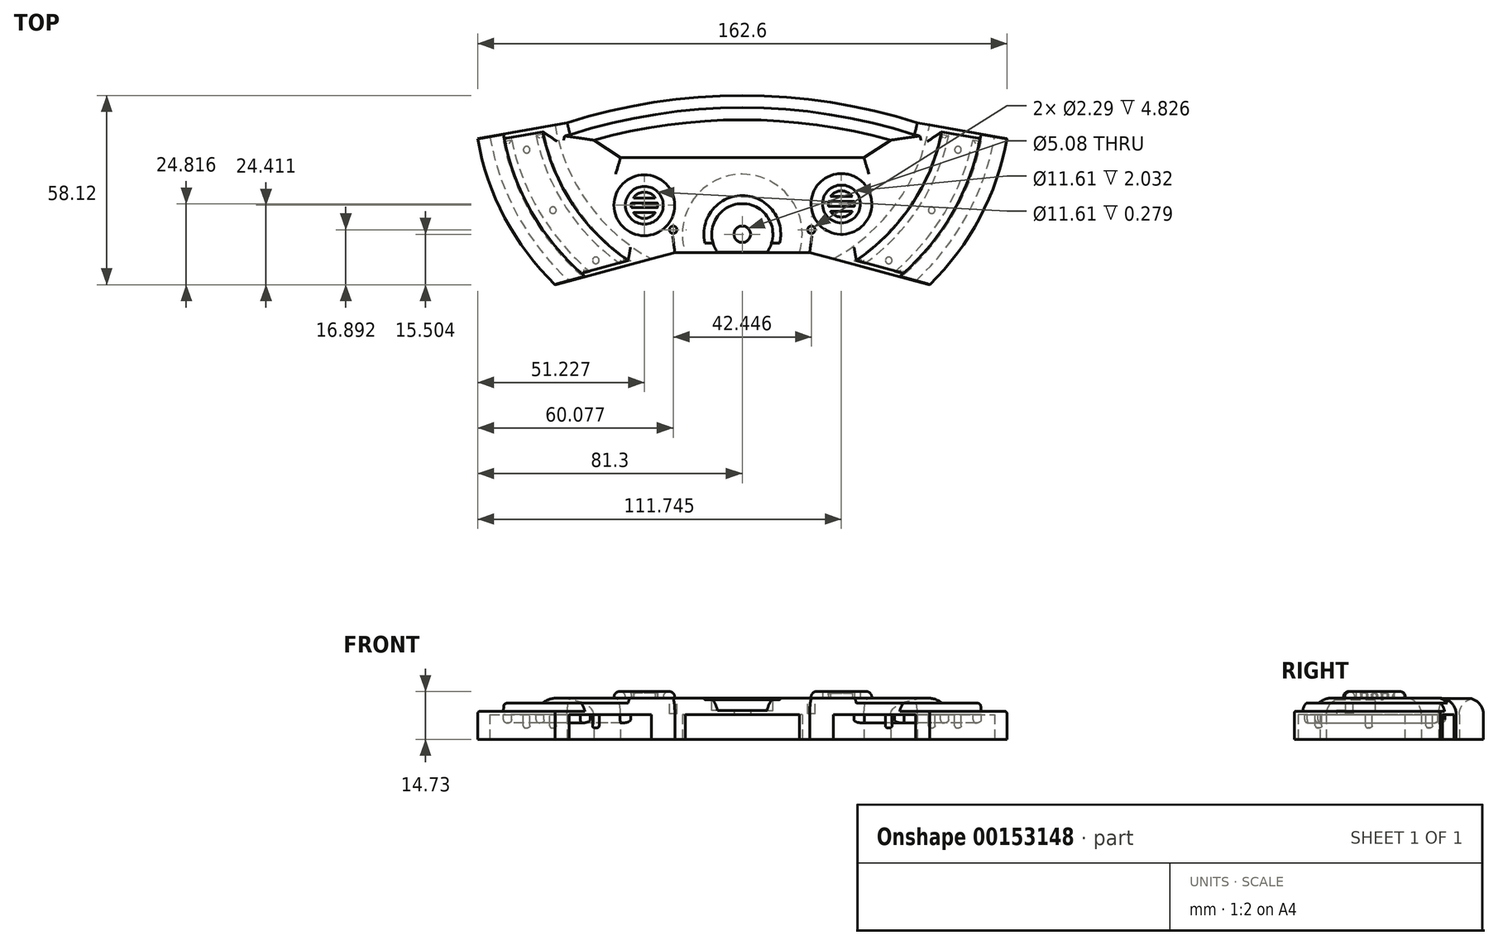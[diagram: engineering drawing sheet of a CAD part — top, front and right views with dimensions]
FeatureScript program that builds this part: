
annotation { "Feature Type Name" : "Feature", "Feature Type Description" : "" }
export const myFeature = defineFeature(function(context is Context, id is Id, definition is map)
    precondition{}
    {
        {
            var Q0;
            Q0=qCreatedBy(makeId("Top.planeOp"),FACE);
            var sketch = newSketch(context, id + "F0", { "sketchPlane" : qUnion([Q0])});
            skCircle(sketch, "E0", {"center": v(0, 0) * mm, "radius": 76.2 * mm, "construction": true});
            skCircle(sketch, "E1", {"center": v(0, 0) * mm, "radius": 60.96 * mm, "construction": true});
            skArc(sketch, "E2", {"start": v(-81.3, -14.33) * mm, "mid": v(-72.94, -38.65) * mm, "end": v(-57.5, -59.22) * mm});
            skLineSegment(sketch, "E3", {"start": v(0, 0) * mm, "end": v(-81.3, -14.33) * mm, "construction": true});
            skArc(sketch, "E4", {"start": v(81.3, -14.33) * mm, "mid": v(72.94, -38.65) * mm, "end": v(57.5, -59.22) * mm});
            skLineSegment(sketch, "E5", {"start": v(81.3, -14.33) * mm, "end": v(0, 0) * mm, "construction": true});
            skLineSegment(sketch, "E6", {"start": v(81.3, -14.33) * mm, "end": v(57.5, -59.22) * mm, "construction": true});
            skLineSegment(sketch, "E7", {"start": v(-81.3, -14.33) * mm, "end": v(-57.5, -59.22) * mm, "construction": true});
            skLineSegment(sketch, "E8", {"start": v(57.5, -59.22) * mm, "end": v(20.7, -49.36) * mm});
            skLineSegment(sketch, "E9", {"start": v(20.7, -49.36) * mm, "end": v(-20.7, -49.36) * mm});
            skLineSegment(sketch, "E10", {"start": v(-20.7, -49.36) * mm, "end": v(-57.5, -59.22) * mm});
            skLineSegment(sketch, "E11", {"start": v(-81.3, -14.33) * mm, "end": v(-53.78, -9.48) * mm});
            skLineSegment(sketch, "E12", {"start": v(-45.58, -14.8) * mm, "end": v(-37.38, -20.13) * mm});
            skLineSegment(sketch, "E13", {"start": v(-37.38, -20.13) * mm, "end": v(37.38, -20.13) * mm});
            skLineSegment(sketch, "E14", {"start": v(37.38, -20.13) * mm, "end": v(45.58, -14.8) * mm});
            skLineSegment(sketch, "E15", {"start": v(53.78, -9.48) * mm, "end": v(81.3, -14.33) * mm});
            skLineSegment(sketch, "E16", {"start": v(0, 0) * mm, "end": v(0, -177.8) * mm, "construction": true});
            skArc(sketch, "E17", {"start": v(-53.78, -9.48) * mm, "mid": v(0, -1.1) * mm, "end": v(53.78, -9.48) * mm});
            skArc(sketch, "E18", {"start": v(45.58, -14.8) * mm, "mid": v(0, -8.56) * mm, "end": v(-45.58, -14.8) * mm});
            skSolve(sketch);
        }
        {
            var Q0;
            Q0=qSketchRegion(id+"F0",true);
            extrude(context, id + "F1", {"entities" : qUnion([Q0]), "depth" : 12.7 * mm});
        }
        {
            var Q0;
            Q0=qCreatedBy(makeId("Front.planeOp"),FACE);
            var sketch = newSketch(context, id + "F2", { "sketchPlane" : qUnion([Q0])});
            skLineSegment(sketch, "E19", {"start": v(62.5, 16.37) * mm, "end": v(62.5, 11.1) * mm});
            skLineSegment(sketch, "E20", {"start": v(62.5, 11.1) * mm, "end": v(74.5, 11.1) * mm});
            skLineSegment(sketch, "E21", {"start": v(74.5, 11.1) * mm, "end": v(74.5, 8.65) * mm});
            skLineSegment(sketch, "E22", {"start": v(74.5, 8.65) * mm, "end": v(83.99, 8.65) * mm});
            skLineSegment(sketch, "E23", {"start": v(83.99, 8.65) * mm, "end": v(83.99, 15.75) * mm});
            skLineSegment(sketch, "E24", {"start": v(83.99, 15.75) * mm, "end": v(62.5, 16.37) * mm});
            skSolve(sketch);
        }
        {
            var Q0;
            Q0=qCreatedBy(makeId("Front.planeOp"),FACE);
            var sketch = newSketch(context, id + "F3", { "sketchPlane" : qUnion([Q0])});
            skLineSegment(sketch, "E25", {"start": v(0, 99.5) * mm, "end": v(0, -112.08) * mm, "construction": true});
            skSolve(sketch);
        }
        {
            var Q0;
            Q0=qSketchRegion(id+"F2",true);
            var Q1;
            Q1=sQuery(id+"F3.wireOp",EDGE,"E25");
            revolve(context, id + "F4", {"operationType" : NewBodyOperationType.REMOVE, "entities" : qUnion([Q0]), "axis" : qUnion([Q1]), "revolveType" : RevolveType.FULL, "oppositeDirection" : true});
        }
        {
            var Q0;
            Q0=makeQuery(id+"F1.opExtrude","CAP_FACE",FACE,{"disambiguationData":[OSD([sQuery(id+"F0.wireOp",EDGE,"E2"),sQuery(id+"F0.wireOp",EDGE,"E4"),sQuery(id+"F0.wireOp",EDGE,"E8"),sQuery(id+"F0.wireOp",EDGE,"E9"),sQuery(id+"F0.wireOp",EDGE,"E10"),sQuery(id+"F0.wireOp",EDGE,"E11"),sQuery(id+"F0.wireOp",EDGE,"E12"),sQuery(id+"F0.wireOp",EDGE,"E13"),sQuery(id+"F0.wireOp",EDGE,"E14"),sQuery(id+"F0.wireOp",EDGE,"E15"),sQuery(id+"F0.wireOp",EDGE,"E17"),sQuery(id+"F0.wireOp",EDGE,"E18")])],"isStart":false});
            fillet(context, id + "F5", {"entities" : qUnion([Q0]), "radius" : 5.08 * mm, "tangentPropagation" : true, "allowEdgeOverflow" : false});
        }
        {
            var Q0;
            Q0=makeQuery(id+"F1.opExtrude","CAP_FACE",FACE,{"disambiguationData":[OSD([sQuery(id+"F0.wireOp",EDGE,"E2"),sQuery(id+"F0.wireOp",EDGE,"E4"),sQuery(id+"F0.wireOp",EDGE,"E8"),sQuery(id+"F0.wireOp",EDGE,"E9"),sQuery(id+"F0.wireOp",EDGE,"E10"),sQuery(id+"F0.wireOp",EDGE,"E11"),sQuery(id+"F0.wireOp",EDGE,"E12"),sQuery(id+"F0.wireOp",EDGE,"E13"),sQuery(id+"F0.wireOp",EDGE,"E14"),sQuery(id+"F0.wireOp",EDGE,"E15"),sQuery(id+"F0.wireOp",EDGE,"E17"),sQuery(id+"F0.wireOp",EDGE,"E18")])],"isStart":false});
            var sketch = newSketch(context, id + "F6", { "sketchPlane" : qUnion([Q0])});
            skLineSegment(sketch, "E26", {"start": v(38.88, -25.21) * mm, "end": v(34.33, -47.75) * mm, "construction": true});
            skLineSegment(sketch, "E27", {"start": v(34.33, -47.75) * mm, "end": v(56.82, -15.18) * mm, "construction": true});
            skLineSegment(sketch, "E28", {"start": v(56.82, -15.18) * mm, "end": v(-56.82, -15.18) * mm, "construction": true});
            skLineSegment(sketch, "E29", {"start": v(-56.82, -15.18) * mm, "end": v(-34.33, -47.75) * mm, "construction": true});
            skLineSegment(sketch, "E30", {"start": v(-34.33, -47.75) * mm, "end": v(-38.88, -25.21) * mm, "construction": true});
            skLineSegment(sketch, "E31", {"start": v(-38.88, -25.21) * mm, "end": v(46.13, -36.48) * mm, "construction": true});
            skPoint(sketch, "E31.endSnap0", {"position": v(-36.6, -36.48) * mm});
            skLineSegment(sketch, "E32", {"start": v(46.13, -36.48) * mm, "end": v(-42.1, -36.48) * mm, "construction": true});
            skLineSegment(sketch, "E33", {"start": v(-42.1, -36.48) * mm, "end": v(38.88, -25.21) * mm, "construction": true});
            skLineSegment(sketch, "E34", {"start": v(21.38, -44.28) * mm, "end": v(38.88, -25.21) * mm, "construction": true});
            skLineSegment(sketch, "E35", {"start": v(-21.38, -44.28) * mm, "end": v(-38.88, -25.21) * mm, "construction": true});
            skCircle(sketch, "E36", {"center": v(30.44, -34.4) * mm, "radius": 9.33 * mm});
            skCircle(sketch, "E37", {"center": v(-30.07, -34.8) * mm, "radius": 9.33 * mm});
            skCircle(sketch, "E38", {"center": v(-30.07, -34.8) * mm, "radius": 5.8 * mm});
            skCircle(sketch, "E39", {"center": v(30.44, -34.4) * mm, "radius": 5.8 * mm});
            skSolve(sketch);
        }
        {
            var Q0;
            Q0=qSketchRegion(id+"F6",true);
            extrude(context, id + "F7", {"entities" : qUnion([Q0]), "operationType" : NewBodyOperationType.ADD, "depth" : 2.03 * mm});
        }
        {
            var Q0;
            Q0=makeQuery(id+"F7.opExtrude","CAP_FACE",FACE,{"disambiguationData":[OSD([sQuery(id+"F6.wireOp",EDGE,"E37"),sQuery(id+"F6.wireOp",EDGE,"E38")])],"isStart":false});
            var Q1;
            Q1=makeQuery(id+"F7.opExtrude","CAP_EDGE",EDGE,{"disambiguationData":[OSD([sQuery(id+"F6.wireOp",EDGE,"E36")])],"isStart":false});
            fillet(context, id + "F8", {"entities" : qUnion([Q0, Q1]), "radius" : 1.75 * mm, "tangentPropagation" : true, "allowEdgeOverflow" : false});
        }
        {
            var Q0;
            Q0=makeQuery(id+"F7.boolean.opBoolean","SPLIT",FACE,{"disambiguationData":[TD([makeQuery(id+"F7.opExtrude","SWEPT_FACE",FACE,{"disambiguationData":[OSD([sQuery(id+"F6.wireOp",EDGE,"E38")])]})])],"derivedFrom":makeQuery(id+"F1.opExtrude","CAP_FACE",FACE,{"disambiguationData":[OSD([sQuery(id+"F0.wireOp",EDGE,"E2"),sQuery(id+"F0.wireOp",EDGE,"E4"),sQuery(id+"F0.wireOp",EDGE,"E8"),sQuery(id+"F0.wireOp",EDGE,"E9"),sQuery(id+"F0.wireOp",EDGE,"E10"),sQuery(id+"F0.wireOp",EDGE,"E11"),sQuery(id+"F0.wireOp",EDGE,"E12"),sQuery(id+"F0.wireOp",EDGE,"E13"),sQuery(id+"F0.wireOp",EDGE,"E14"),sQuery(id+"F0.wireOp",EDGE,"E15"),sQuery(id+"F0.wireOp",EDGE,"E17"),sQuery(id+"F0.wireOp",EDGE,"E18")])],"isStart":false})});
            var sketch = newSketch(context, id + "F9", { "sketchPlane" : qUnion([Q0])});
            skArc(sketch, "E40", {"start": v(-34.04, -34.07) * mm, "mid": v(-34.11, -34.8) * mm, "end": v(-34.04, -35.55) * mm});
            skLineSegment(sketch, "E41", {"start": v(-26.73, -32.55) * mm, "end": v(-33.42, -32.55) * mm});
            skLineSegment(sketch, "E42", {"start": v(-26.1, -34.07) * mm, "end": v(-34.04, -34.07) * mm});
            skLineSegment(sketch, "E43", {"start": v(-26.1, -35.55) * mm, "end": v(-34.04, -35.55) * mm});
            skLineSegment(sketch, "E44", {"start": v(-33.42, -37.07) * mm, "end": v(-26.73, -37.07) * mm});
            skArc(sketch, "E45.trimOffspring", {"start": v(-26.73, -32.55) * mm, "mid": v(-30.07, -30.77) * mm, "end": v(-33.42, -32.55) * mm});
            skArc(sketch, "E46.trimOffspring", {"start": v(-26.1, -35.55) * mm, "mid": v(-26.03, -34.8) * mm, "end": v(-26.1, -34.07) * mm});
            skArc(sketch, "E47.trimOffspring", {"start": v(-33.42, -37.07) * mm, "mid": v(-30.07, -38.85) * mm, "end": v(-26.73, -37.07) * mm});
            skSolve(sketch);
        }
        {
            var Q0;
            Q0=makeQuery(id+"F7.boolean.opBoolean","SPLIT",FACE,{"disambiguationData":[TD([makeQuery(id+"F7.opExtrude","SWEPT_FACE",FACE,{"disambiguationData":[OSD([sQuery(id+"F6.wireOp",EDGE,"E39")])]})])],"derivedFrom":makeQuery(id+"F1.opExtrude","CAP_FACE",FACE,{"disambiguationData":[OSD([sQuery(id+"F0.wireOp",EDGE,"E2"),sQuery(id+"F0.wireOp",EDGE,"E4"),sQuery(id+"F0.wireOp",EDGE,"E8"),sQuery(id+"F0.wireOp",EDGE,"E9"),sQuery(id+"F0.wireOp",EDGE,"E10"),sQuery(id+"F0.wireOp",EDGE,"E11"),sQuery(id+"F0.wireOp",EDGE,"E12"),sQuery(id+"F0.wireOp",EDGE,"E13"),sQuery(id+"F0.wireOp",EDGE,"E14"),sQuery(id+"F0.wireOp",EDGE,"E15"),sQuery(id+"F0.wireOp",EDGE,"E17"),sQuery(id+"F0.wireOp",EDGE,"E18")])],"isStart":false})});
            var sketch = newSketch(context, id + "F10", { "sketchPlane" : qUnion([Q0])});
            skArc(sketch, "E48", {"start": v(33.8, -32.14) * mm, "mid": v(30.44, -30.37) * mm, "end": v(27.1, -32.14) * mm});
            skLineSegment(sketch, "E49", {"start": v(27.1, -32.14) * mm, "end": v(33.8, -32.14) * mm});
            skLineSegment(sketch, "E50", {"start": v(34.42, -33.67) * mm, "end": v(26.47, -33.67) * mm});
            skLineSegment(sketch, "E51", {"start": v(26.47, -35.14) * mm, "end": v(34.42, -35.14) * mm});
            skLineSegment(sketch, "E52", {"start": v(33.8, -36.67) * mm, "end": v(27.1, -36.67) * mm});
            skArc(sketch, "E53.trimOffspring", {"start": v(26.47, -33.67) * mm, "mid": v(26.4, -34.4) * mm, "end": v(26.47, -35.14) * mm});
            skArc(sketch, "E54.trimOffspring", {"start": v(27.1, -36.67) * mm, "mid": v(30.44, -38.44) * mm, "end": v(33.8, -36.67) * mm});
            skArc(sketch, "E55.trimOffspring", {"start": v(34.42, -35.14) * mm, "mid": v(34.48, -34.4) * mm, "end": v(34.42, -33.67) * mm});
            skSolve(sketch);
        }
        {
            var Q0;
            Q0=qSketchRegion(id+"F9",true);
            extrude(context, id + "F11", {"entities" : qUnion([Q0]), "operationType" : NewBodyOperationType.ADD, "depth" : 1.52 * mm});
        }
        {
            var Q0;
            Q0=makeQuery(id+"F11.opExtrude","CAP_EDGE",EDGE,{"disambiguationData":[OSD([sQuery(id+"F9.wireOp",EDGE,"E42")])],"isStart":false});
            var Q1;
            Q1=makeQuery(id+"F11.opExtrude","CAP_EDGE",EDGE,{"disambiguationData":[OSD([sQuery(id+"F9.wireOp",EDGE,"E43")])],"isStart":false});
            fillet(context, id + "F12", {"entities" : qUnion([Q0, Q1]), "radius" : 0.7 * mm, "tangentPropagation" : true, "allowEdgeOverflow" : false});
        }
        {
            var Q0;
            Q0=makeQuery(id+"F11.opExtrude","CAP_FACE",FACE,{"disambiguationData":[OSD([sQuery(id+"F9.wireOp",EDGE,"E41"),sQuery(id+"F9.wireOp",EDGE,"E45.trimOffspring")])],"isStart":false});
            var Q1;
            Q1=makeQuery(id+"F11.opExtrude","CAP_FACE",FACE,{"disambiguationData":[OSD([sQuery(id+"F9.wireOp",EDGE,"E44"),sQuery(id+"F9.wireOp",EDGE,"E47.trimOffspring")])],"isStart":false});
            fillet(context, id + "F13", {"entities" : qUnion([Q0, Q1]), "radius" : 0.25 * mm, "tangentPropagation" : true, "allowEdgeOverflow" : false});
        }
        {
            var Q0;
            Q0=qSketchRegion(id+"F10",true);
            extrude(context, id + "F14", {"entities" : qUnion([Q0]), "operationType" : NewBodyOperationType.ADD, "depth" : 1.52 * mm});
        }
        {
            var Q0;
            Q0=makeQuery(id+"F4.boolean.opBoolean","COPY",EDGE,{"disambiguationData":[OD(1.0)],"derivedFrom":makeQuery(id+"F4.opRevolve","SWEPT_EDGE",EDGE,{"disambiguationData":[OSD([sQuery(id+"F2.wireOp",EDGE,"E20"),sQuery(id+"F2.wireOp",EDGE,"E21")])]})});
            var Q1;
            Q1=makeQuery(id+"F4.boolean.opBoolean","INTERSECT",EDGE,{"derivedFrom":[makeQuery(id+"F1.opExtrude","SWEPT_FACE",FACE,{"disambiguationData":[OSD([sQuery(id+"F0.wireOp",EDGE,"E2")])]}),makeQuery(id+"F4.opRevolve","SWEPT_FACE",FACE,{"disambiguationData":[OSD([sQuery(id+"F2.wireOp",EDGE,"E22")])]})]});
            var Q2;
            Q2=makeQuery(id+"F4.boolean.opBoolean","COPY",EDGE,{"disambiguationData":[OD(0.0)],"derivedFrom":makeQuery(id+"F4.opRevolve","SWEPT_EDGE",EDGE,{"disambiguationData":[OSD([sQuery(id+"F2.wireOp",EDGE,"E20"),sQuery(id+"F2.wireOp",EDGE,"E21")])]})});
            var Q3;
            Q3=makeQuery(id+"F4.boolean.opBoolean","INTERSECT",EDGE,{"derivedFrom":[makeQuery(id+"F1.opExtrude","SWEPT_FACE",FACE,{"disambiguationData":[OSD([sQuery(id+"F0.wireOp",EDGE,"E4")])]}),makeQuery(id+"F4.opRevolve","SWEPT_FACE",FACE,{"disambiguationData":[OSD([sQuery(id+"F2.wireOp",EDGE,"E22")])]})]});
            fillet(context, id + "F15", {"entities" : qUnion([Q0, Q1, Q2, Q3]), "radius" : 0.76 * mm, "tangentPropagation" : true, "allowEdgeOverflow" : false});
        }
        {
            var Q0;
            Q0=qCreatedBy(makeId("Top.planeOp"),FACE);
            var sketch = newSketch(context, id + "F16", { "sketchPlane" : qUnion([Q0])});
            skCircle(sketch, "E56", {"center": v(0, 0) * mm, "radius": 78.74 * mm});
            skCircle(sketch, "E57", {"center": v(0, 0) * mm, "radius": 58.42 * mm});
            skSolve(sketch);
        }
        {
            var Q0;
            Q0=qSketchRegion(id+"F16",true);
            extrude(context, id + "F17", {"entities" : qUnion([Q0]), "operationType" : NewBodyOperationType.REMOVE, "depth" : 7.62 * mm});
        }
        {
            var Q0;
            Q0=makeQuery(id+"F14.opExtrude","CAP_EDGE",EDGE,{"disambiguationData":[OSD([sQuery(id+"F10.wireOp",EDGE,"E50")])],"isStart":false});
            var Q1;
            Q1=makeQuery(id+"F14.opExtrude","CAP_EDGE",EDGE,{"disambiguationData":[OSD([sQuery(id+"F10.wireOp",EDGE,"E51")])],"isStart":false});
            fillet(context, id + "F18", {"entities" : qUnion([Q0, Q1]), "radius" : 0.71 * mm, "tangentPropagation" : true, "allowEdgeOverflow" : false});
        }
        {
            var Q0;
            Q0=makeQuery(id+"F14.opExtrude","CAP_FACE",FACE,{"disambiguationData":[OSD([sQuery(id+"F10.wireOp",EDGE,"E48"),sQuery(id+"F10.wireOp",EDGE,"E49")])],"isStart":false});
            var Q1;
            Q1=makeQuery(id+"F14.opExtrude","CAP_FACE",FACE,{"disambiguationData":[OSD([sQuery(id+"F10.wireOp",EDGE,"E52"),sQuery(id+"F10.wireOp",EDGE,"E54.trimOffspring")])],"isStart":false});
            fillet(context, id + "F19", {"entities" : qUnion([Q0, Q1]), "radius" : 0.25 * mm, "tangentPropagation" : true, "allowEdgeOverflow" : false});
        }
        {
            var Q0;
            Q0=makeQuery(id+"F17.boolean.opBoolean","COPY",FACE,{"disambiguationData":[OD(1.0)],"derivedFrom":makeQuery(id+"F17.opExtrude","CAP_FACE",FACE,{"disambiguationData":[OSD([sQuery(id+"F16.wireOp",EDGE,"E56"),sQuery(id+"F16.wireOp",EDGE,"E57")])],"isStart":false})});
            var sketch = newSketch(context, id + "F20", { "sketchPlane" : qUnion([Q0])});
            skCircle(sketch, "E58", {"center": v(0, 0) * mm, "radius": 76.2 * mm, "construction": true});
            skCircle(sketch, "E59", {"center": v(0, 0) * mm, "radius": 60.96 * mm, "construction": true});
            skLineSegment(sketch, "E60", {"start": v(0, 0) * mm, "end": v(66.24, 17.75) * mm, "construction": true});
            skCircle(sketch, "E61", {"center": v(0, 0) * mm, "radius": 68.58 * mm, "construction": true});
            skLineSegment(sketch, "E62", {"start": v(0, 0) * mm, "end": v(58.16, 36.34) * mm, "construction": true});
            skLineSegment(sketch, "E63", {"start": v(0, 0) * mm, "end": v(45, 51.76) * mm, "construction": true});
            skCircle(sketch, "E64", {"center": v(66.24, 17.75) * mm, "radius": 1.02 * mm});
            skCircle(sketch, "E65", {"center": v(58.16, 36.34) * mm, "radius": 1.02 * mm});
            skCircle(sketch, "E66", {"center": v(45, 51.76) * mm, "radius": 1.02 * mm});
            skCircle(sketch, "E67.MirrorC", {"center": v(-66.24, 17.75) * mm, "radius": 1.02 * mm});
            skCircle(sketch, "E68.MirrorC", {"center": v(-58.16, 36.34) * mm, "radius": 1.02 * mm});
            skCircle(sketch, "E69.MirrorC", {"center": v(-45, 51.76) * mm, "radius": 1.02 * mm});
            skSolve(sketch);
        }
        {
            var Q0;
            Q0=qSketchRegion(id+"F20",true);
            extrude(context, id + "F21", {"entities" : qUnion([Q0]), "operationType" : NewBodyOperationType.ADD, "depth" : 4.06 * mm});
        }
        {
            var Q0;
            Q0=makeQuery(id+"F21.opExtrude","CAP_EDGE",EDGE,{"disambiguationData":[OSD([sQuery(id+"F20.wireOp",EDGE,"E69.MirrorC")])],"isStart":false});
            var Q1;
            Q1=makeQuery(id+"F21.opExtrude","CAP_EDGE",EDGE,{"disambiguationData":[OSD([sQuery(id+"F20.wireOp",EDGE,"E68.MirrorC")])],"isStart":false});
            var Q2;
            Q2=makeQuery(id+"F21.opExtrude","CAP_FACE",FACE,{"disambiguationData":[OSD([sQuery(id+"F20.wireOp",EDGE,"E67.MirrorC")])],"isStart":false});
            var Q3;
            Q3=makeQuery(id+"F21.opExtrude","CAP_FACE",FACE,{"disambiguationData":[OSD([sQuery(id+"F20.wireOp",EDGE,"E66")])],"isStart":false});
            var Q4;
            Q4=makeQuery(id+"F21.opExtrude","CAP_EDGE",EDGE,{"disambiguationData":[OSD([sQuery(id+"F20.wireOp",EDGE,"E65")])],"isStart":false});
            var Q5;
            Q5=makeQuery(id+"F21.opExtrude","CAP_EDGE",EDGE,{"disambiguationData":[OSD([sQuery(id+"F20.wireOp",EDGE,"E64")])],"isStart":false});
            fillet(context, id + "F22", {"entities" : qUnion([Q0, Q1, Q2, Q3, Q4, Q5]), "radius" : 0.64 * mm, "tangentPropagation" : true, "allowEdgeOverflow" : false});
        }
        {
            var Q0;
            Q0=makeQuery(id+"F17.boolean.opBoolean","COPY",FACE,{"disambiguationData":[OD(1.0)],"derivedFrom":makeQuery(id+"F17.opExtrude","CAP_FACE",FACE,{"disambiguationData":[OSD([sQuery(id+"F16.wireOp",EDGE,"E56"),sQuery(id+"F16.wireOp",EDGE,"E57")])],"isStart":false})});
            var sketch = newSketch(context, id + "F23", { "sketchPlane" : qUnion([Q0])});
            skArc(sketch, "E70", {"start": v(-37.52, 52.8) * mm, "mid": v(-54.16, 35.52) * mm, "end": v(-63.37, 13.37) * mm});
            skArc(sketch, "E71", {"start": v(-46.75, 55.27) * mm, "mid": v(-62.21, 37.01) * mm, "end": v(-70.88, 14.7) * mm});
            skArc(sketch, "E72", {"start": v(-49.71, 56.07) * mm, "mid": v(-64.86, 37.52) * mm, "end": v(-73.38, 15.15) * mm});
            skLineSegment(sketch, "E73", {"start": v(-53.19, 58.06) * mm, "end": v(-14.7, 47.75) * mm, "construction": true});
            skLineSegment(sketch, "E74.MirrorCS", {"start": v(53.19, 58.06) * mm, "end": v(14.7, 47.75) * mm, "construction": true});
            skLineSegment(sketch, "E75", {"start": v(-77.54, 13.67) * mm, "end": v(-57.53, 10.14) * mm, "construction": true});
            skLineSegment(sketch, "E76.MirrorCS", {"start": v(77.54, 13.67) * mm, "end": v(57.53, 10.14) * mm, "construction": true});
            skArc(sketch, "E77.trimOffspring", {"start": v(63.37, 13.37) * mm, "mid": v(54.16, 35.52) * mm, "end": v(37.52, 52.8) * mm});
            skArc(sketch, "E78.trimOffspring", {"start": v(73.38, 15.15) * mm, "mid": v(64.86, 37.52) * mm, "end": v(49.71, 56.07) * mm});
            skArc(sketch, "E79.trimOffspring", {"start": v(70.88, 14.7) * mm, "mid": v(62.21, 37.01) * mm, "end": v(46.75, 55.27) * mm});
            skLineSegment(sketch, "E80", {"start": v(-54.08, 57.23) * mm, "end": v(-15.24, 46.83) * mm, "construction": true});
            skLineSegment(sketch, "E81", {"start": v(-77.13, 15.82) * mm, "end": v(-46.34, 10.34) * mm, "construction": true});
            skLineSegment(sketch, "E82.MirrorCS", {"start": v(54.08, 57.23) * mm, "end": v(37.52, 52.8) * mm, "construction": true});
            skLineSegment(sketch, "E83.MirrorCS", {"start": v(77.13, 15.82) * mm, "end": v(65.88, 13.82) * mm, "construction": true});
            skLineSegment(sketch, "E84", {"start": v(-49.71, 56.07) * mm, "end": v(-46.75, 55.27) * mm});
            skLineSegment(sketch, "E85", {"start": v(-40.66, 53.64) * mm, "end": v(-37.52, 52.8) * mm});
            skLineSegment(sketch, "E86", {"start": v(-73.38, 15.15) * mm, "end": v(-70.88, 14.7) * mm});
            skLineSegment(sketch, "E87", {"start": v(-65.88, 13.82) * mm, "end": v(-63.37, 13.37) * mm});
            skLineSegment(sketch, "E88", {"start": v(63.37, 13.37) * mm, "end": v(65.88, 13.82) * mm});
            skLineSegment(sketch, "E89", {"start": v(70.88, 14.7) * mm, "end": v(73.38, 15.15) * mm});
            skLineSegment(sketch, "E90", {"start": v(37.52, 52.8) * mm, "end": v(40.66, 53.64) * mm});
            skLineSegment(sketch, "E91", {"start": v(46.75, 55.27) * mm, "end": v(49.71, 56.07) * mm});
            skArc(sketch, "E92", {"start": v(60.87, 12.93) * mm, "mid": v(51.42, 35.05) * mm, "end": v(34.29, 51.93) * mm});
            skArc(sketch, "E93", {"start": v(-36.4, 53.57) * mm, "mid": v(0, -64.77) * mm, "end": v(36.4, 53.57) * mm, "construction": true});
            skLineSegment(sketch, "E94.trimOffspring", {"start": v(63.37, 13.37) * mm, "end": v(46.34, 10.34) * mm, "construction": true});
            skLineSegment(sketch, "E95.trimOffspring", {"start": v(34.29, 51.93) * mm, "end": v(15.24, 46.83) * mm, "construction": true});
            skArc(sketch, "E96.trimOffspring", {"start": v(-34.29, 51.93) * mm, "mid": v(-51.42, 35.05) * mm, "end": v(-60.87, 12.93) * mm});
            skLineSegment(sketch, "E97", {"start": v(-34.29, 51.93) * mm, "end": v(-37.52, 52.8) * mm});
            skLineSegment(sketch, "E98", {"start": v(-60.87, 12.93) * mm, "end": v(-63.37, 13.37) * mm});
            skLineSegment(sketch, "E99", {"start": v(60.87, 12.93) * mm, "end": v(63.37, 13.37) * mm});
            skLineSegment(sketch, "E100", {"start": v(34.29, 51.93) * mm, "end": v(37.52, 52.8) * mm});
            skSolve(sketch);
        }
        {
            var Q0;
            Q0=qSketchRegion(id+"F23",true);
            extrude(context, id + "F24", {"entities" : qUnion([Q0]), "operationType" : NewBodyOperationType.ADD, "depth" : 2.54 * mm});
        }
        {
            var Q0;
            Q0=makeQuery(id+"F24.opExtrude","CAP_FACE",FACE,{"disambiguationData":[OSD([sQuery(id+"F23.wireOp",EDGE,"e2b732bb-df48-4231-8cf6-9f20eeaedfbb.trimOffspring"),sQuery(id+"F23.wireOp",EDGE,"E77.trimOffspring"),sQuery(id+"F23.wireOp",EDGE,"E88"),sQuery(id+"F23.wireOp",EDGE,"E90")])],"isStart":false});
            var Q1;
            Q1=makeQuery(id+"F24.opExtrude","CAP_FACE",FACE,{"disambiguationData":[OSD([sQuery(id+"F23.wireOp",EDGE,"E78.trimOffspring"),sQuery(id+"F23.wireOp",EDGE,"E79.trimOffspring"),sQuery(id+"F23.wireOp",EDGE,"E89"),sQuery(id+"F23.wireOp",EDGE,"E91")])],"isStart":false});
            var Q2;
            Q2=makeQuery(id+"F24.opExtrude","CAP_FACE",FACE,{"disambiguationData":[OSD([sQuery(id+"F23.wireOp",EDGE,"E71"),sQuery(id+"F23.wireOp",EDGE,"E72"),sQuery(id+"F23.wireOp",EDGE,"E84"),sQuery(id+"F23.wireOp",EDGE,"E86")])],"isStart":false});
            var Q3;
            Q3=makeQuery(id+"F24.opExtrude","CAP_FACE",FACE,{"disambiguationData":[OSD([sQuery(id+"F23.wireOp",EDGE,"HvzRBNUH-Ws5O-fryz-vqn3-pfWEQRTrrrLi"),sQuery(id+"F23.wireOp",EDGE,"E70"),sQuery(id+"F23.wireOp",EDGE,"E85"),sQuery(id+"F23.wireOp",EDGE,"E87")])],"isStart":false});
            fillet(context, id + "F25", {"entities" : qUnion([Q0, Q1, Q2, Q3]), "radius" : 1.02 * mm, "tangentPropagation" : true, "allowEdgeOverflow" : false});
        }
        {
            var Q0;
            {var subQ0=sQuery(id+"F0.wireOp",EDGE,"E18");var subQ1=sQuery(id+"F0.wireOp",EDGE,"E15");var subQ2=sQuery(id+"F0.wireOp",EDGE,"E14");var subQ3=sQuery(id+"F0.wireOp",EDGE,"E13");var subQ4=sQuery(id+"F0.wireOp",EDGE,"E12");var subQ5=sQuery(id+"F0.wireOp",EDGE,"E8");var subQ6=sQuery(id+"F0.wireOp",EDGE,"E17");var subQ7=sQuery(id+"F0.wireOp",EDGE,"E9");var subQ8=sQuery(id+"F0.wireOp",EDGE,"E10");var subQ9=sQuery(id+"F0.wireOp",EDGE,"E11");Q0=makeQuery(id+"F17.boolean.opBoolean","SPLIT",FACE,{"disambiguationData":[TD([makeQuery(id+"F1.opExtrude","SWEPT_FACE",FACE,{"disambiguationData":[OSD([subQ7])]})])],"derivedFrom":makeQuery(id+"F1.opExtrude","CAP_FACE",FACE,{"disambiguationData":[OSD([sQuery(id+"F0.wireOp",EDGE,"E2"),sQuery(id+"F0.wireOp",EDGE,"E4"),subQ5,subQ7,subQ8,subQ9,subQ4,subQ3,subQ2,subQ1,subQ6,subQ0])],"isStart":true})});}
            var sketch = newSketch(context, id + "F26", { "sketchPlane" : qUnion([Q0])});
            skCircle(sketch, "E101", {"center": v(0, 0) * mm, "radius": 60.96 * mm, "construction": true});
            skCircle(sketch, "E102", {"center": v(0, 0) * mm, "radius": 76.2 * mm, "construction": true});
            skCircle(sketch, "E103", {"center": v(0, 0) * mm, "radius": 58.42 * mm, "construction": true});
            skLineSegment(sketch, "E104", {"start": v(0, 0) * mm, "end": v(0, 98.07) * mm, "construction": true});
            skCircle(sketch, "E105", {"center": v(0, 43.7) * mm, "radius": 18.41 * mm});
            skCircle(sketch, "E106", {"center": v(0, 0) * mm, "radius": 59.7 * mm, "construction": true});
            skSolve(sketch);
        }
        {
            var Q0;
            Q0=qSketchRegion(id+"F26",true);
            extrude(context, id + "F27", {"entities" : qUnion([Q0]), "operationType" : NewBodyOperationType.REMOVE, "oppositeDirection" : true, "depth" : 7.62 * mm});
        }
        {
            var Q0;
            {var subQ0=sQuery(id+"F26.wireOp",EDGE,"E105");var subQ1=makeQuery(id+"F1.opExtrude","CAP_EDGE",EDGE,{"disambiguationData":[OSD([sQuery(id+"F0.wireOp",EDGE,"E9")])],"isStart":true});var subQ2=makeQuery(id+"F26.imprint","INTERSECT",VERTEX,{"disambiguationData":[OD(0.0)],"derivedFrom":[subQ1,subQ0]});Q0=makeQuery(id+"F26.imprint","IMPRINT",FACE,{"disambiguationData":[TD([[makeQuery(id+"F26.imprint","IMPRINT",EDGE,{"disambiguationData":[TD([[subQ2,1.0]])],"derivedFrom":subQ0}),1.0]])]});}
            var sketch = newSketch(context, id + "F28", { "sketchPlane" : qUnion([Q0])});
            skCircle(sketch, "E107", {"center": v(0, 43.72) * mm, "radius": 2.54 * mm});
            skSolve(sketch);
        }
        {
            var Q0;
            Q0=qSketchRegion(id+"F28",true);
            extrude(context, id + "F29", {"entities" : qUnion([Q0]), "operationType" : NewBodyOperationType.REMOVE, "oppositeDirection" : true, "depth" : 25.4 * mm});
        }
        {
            var Q0;
            {var subQ2=sQuery(id+"F0.wireOp",EDGE,"E18");var subQ3=sQuery(id+"F0.wireOp",EDGE,"E17");var subQ4=sQuery(id+"F0.wireOp",EDGE,"E15");var subQ5=sQuery(id+"F0.wireOp",EDGE,"E14");var subQ6=sQuery(id+"F0.wireOp",EDGE,"E13");var subQ7=sQuery(id+"F0.wireOp",EDGE,"E12");var subQ8=sQuery(id+"F0.wireOp",EDGE,"E11");var subQ9=sQuery(id+"F0.wireOp",EDGE,"E10");var subQ10=sQuery(id+"F0.wireOp",EDGE,"E9");var subQ11=sQuery(id+"F0.wireOp",EDGE,"E8");var subQ12=sQuery(id+"F0.wireOp",EDGE,"E4");var subQ13=sQuery(id+"F0.wireOp",EDGE,"E2");var subQ14=makeQuery(id+"F1.opExtrude","CAP_FACE",FACE,{"disambiguationData":[OSD([subQ13,subQ12,subQ11,subQ10,subQ9,subQ8,subQ7,subQ6,subQ5,subQ4,subQ3,subQ2])],"isStart":false});Q0=makeQuery(id+"F7.boolean.opBoolean","SPLIT",FACE,{"disambiguationData":[TD([makeQuery(id+"F5.opFillet","BLEND_FACE",FACE,{"disambiguationData":[OSD([subQ10])]})])],"derivedFrom":subQ14});}
            var sketch = newSketch(context, id + "F30", { "sketchPlane" : qUnion([Q0])});
            skCircle(sketch, "E108", {"center": v(0, -43.72) * mm, "radius": 15.75 * mm, "construction": true});
            skCircle(sketch, "E109", {"center": v(6.93, -29.43) * mm, "radius": 13.34 * mm, "construction": true});
            skCircle(sketch, "E110", {"center": v(-5.47, -24.54) * mm, "radius": 13.34 * mm, "construction": true});
            skSolve(sketch);
        }
        {
            var Q0;
            {var subQ0=sQuery(id+"F6.wireOp",EDGE,"E37");Q0=makeQuery(id+"F30.imprint","IMPRINT",FACE,{"disambiguationData":[TD([[makeQuery(id+"F30.imprint","IMPRINT",EDGE,{"derivedFrom":makeQuery(id+"F7.opExtrude","CAP_EDGE",EDGE,{"disambiguationData":[OSD([subQ0])],"isStart":true})}),-1.0]])]});}
            var sketch = newSketch(context, id + "F31", { "sketchPlane" : qUnion([Q0])});
            skCircle(sketch, "E111", {"center": v(0, -43.63) * mm, "radius": 11.81 * mm});
            skSolve(sketch);
        }
        {
            var Q0;
            Q0 = qSketchRegion(id + "F31", true);
            extrude(context, id + "F32", {"entities" : qUnion([Q0]), "operationType" : NewBodyOperationType.REMOVE, "oppositeDirection" : true, "depth" : 0.5 * mm});
        }
        {
            var Q0;
            Q0=makeQuery(id+"F32.boolean.opBoolean","COPY",FACE,{"derivedFrom":makeQuery(id+"F32.opExtrude","CAP_FACE",FACE,{"disambiguationData":[OSD([sQuery(id+"F31.wireOp",EDGE,"E111")])],"isStart":false})});
            var sketch = newSketch(context, id + "F33", { "sketchPlane" : qUnion([Q0])});
            skCircle(sketch, "E112", {"center": v(0, -43.72) * mm, "radius": 9.4 * mm});
            skSolve(sketch);
        }
        {
            var Q0;
            Q0 = qSketchRegion(id + "F33", true);
            extrude(context, id + "F34", {"entities" : qUnion([Q0]), "operationType" : NewBodyOperationType.REMOVE, "oppositeDirection" : true, "depth" : 3.3 * mm});
        }
        {
            var Q0;
            {var subQ0=sQuery(id+"F6.wireOp",EDGE,"E37");Q0=makeQuery(id+"F30.imprint","IMPRINT",FACE,{"disambiguationData":[TD([[makeQuery(id+"F30.imprint","IMPRINT",EDGE,{"derivedFrom":makeQuery(id+"F7.opExtrude","CAP_EDGE",EDGE,{"disambiguationData":[OSD([subQ0])],"isStart":true})}),-1.0]])]});}
            var sketch = newSketch(context, id + "F35", { "sketchPlane" : qUnion([Q0])});
            skCircle(sketch, "E113", {"center": v(0, -43.85) * mm, "radius": 21.28 * mm, "construction": true});
            skLineSegment(sketch, "E114", {"start": v(-21.22, -42.33) * mm, "end": v(21.22, -42.33) * mm, "construction": true});
            skCircle(sketch, "E115", {"center": v(-21.22, -42.33) * mm, "radius": 1.14 * mm});
            skCircle(sketch, "E116", {"center": v(21.22, -42.33) * mm, "radius": 1.14 * mm});
            skSolve(sketch);
        }
        {
            var Q0;
            Q0 = qSketchRegion(id + "F35", true);
            extrude(context, id + "F36", {"entities" : qUnion([Q0]), "operationType" : NewBodyOperationType.REMOVE, "oppositeDirection" : true, "depth" : 4.83 * mm});
        }
    });
